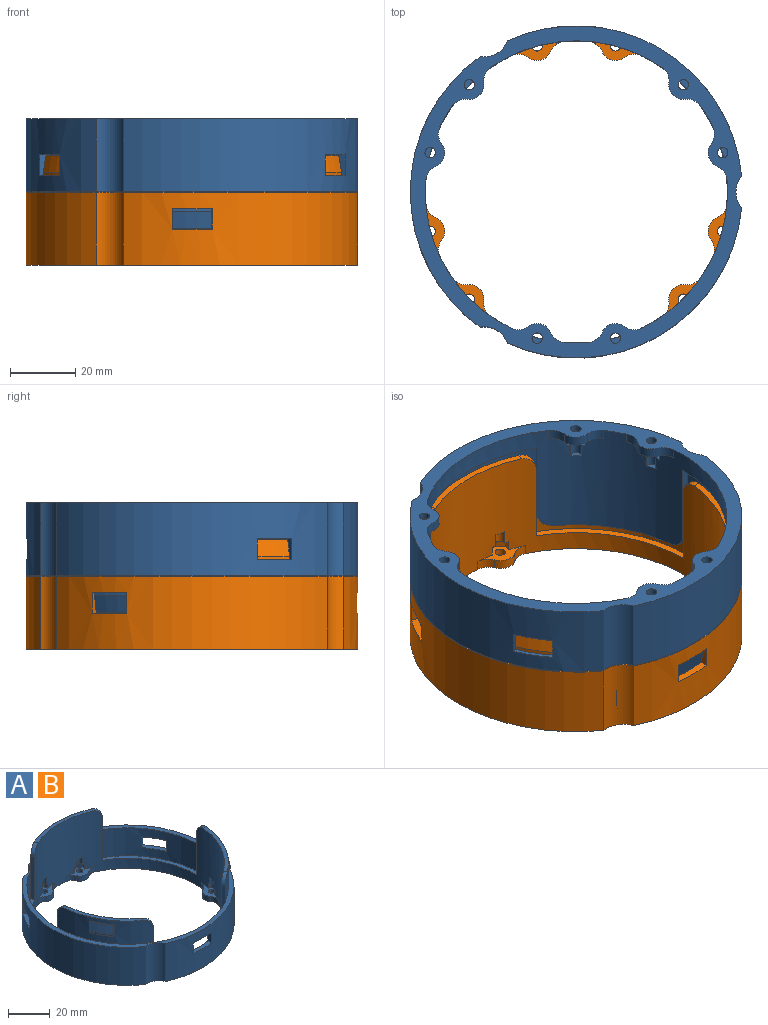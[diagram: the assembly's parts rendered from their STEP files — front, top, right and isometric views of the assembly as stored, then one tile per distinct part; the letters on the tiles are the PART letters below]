
ASSEMBLY  parts=2 mates=1
PART A: 135 faces, bbox 101.8x102x36 mm
  f0: cylinder r=51mm len=71.96mm, axis (0,0,-1), area 2097.8mm2, adj f1,f5,f6,f7,f8,f29,f35,f53
  f1: cylinder r=7.5mm len=22.4mm, axis (0,0,-1), area 235.6mm2, adj f0,f2,f29,f35
  f2: cylinder r=51mm len=83.1mm, axis (0,0,-1), area 2097.8mm2, adj f1,f3,f9,f10,f11,f12,f29,f35
  f3: cylinder r=7.5mm len=22.4mm, axis (0,0,-1), area 235.6mm2, adj f2,f4,f29,f35
  f4: cylinder r=51mm len=71.96mm, axis (0,0,-1), area 2097.8mm2, adj f3,f29,f35,f49,f50,f51,f52,f53
  f5: plane 11.86x8.24mm, normal (0,0,1), area 29.6mm2, adj f0,f7,f8,f37
  f6: plane 11.86x8.24mm, normal (0,0,-1), area 29.6mm2, adj f0,f7,f8,f37
  f7: plane 6.3x2.09mm, normal (0.5,-0.87,0), area 15.2mm2, adj f0,f5,f6,f37
  f8: plane 6.3x2.09mm, normal (-0.5,0.87,0), area 15.2mm2, adj f0,f5,f6,f37
  f9: plane 11.86x8.24mm, normal (0,0,1), area 29.6mm2, adj f2,f11,f12,f44
  f10: plane 11.86x8.24mm, normal (0,0,-1), area 29.6mm2, adj f2,f11,f12,f44
  f11: plane 6.3x2.09mm, normal (0.5,0.87,0), area 15.2mm2, adj f2,f9,f10,f44
  f12: plane 6.3x2.09mm, normal (-0.5,-0.87,0), area 15.2mm2, adj f2,f9,f10,f44
  f13: cylinder r=48.6mm len=48.97mm, axis (0,0,1), area 763.9mm2, adj f29,f41,f42,f43,f49,f50,f51,f52
  f14: cylinder r=49.81mm len=10.39mm, axis (0,0,1), area 12mm2, adj f15,f17,f18,f133
  f15: plane 6x1.23mm, normal (-0.5,0.87,0), area 6mm2, adj f14,f16,f18,f30,f133
  f16: plane 10.6x6.36mm, normal (0,0,1), area 5mm2, adj f15,f17,f30,f133
  f17: plane 6x1.23mm, normal (0.5,-0.87,0), area 6mm2, adj f14,f16,f18,f30,f133
  f18: plane 11.1x7.23mm, normal (0,0,-1), area 17mm2, adj f14,f15,f17,f30
  f19: cylinder r=49.81mm len=10.39mm, axis (0,0,1), area 12mm2, adj f20,f22,f23,f134
  f20: plane 6x1.23mm, normal (-0.5,-0.87,0), area 6mm2, adj f19,f21,f23,f36,f134
  f21: plane 10.6x6.36mm, normal (0,0,1), area 5mm2, adj f20,f22,f36,f134
  f22: plane 6x1.23mm, normal (0.5,0.87,0), area 6mm2, adj f19,f21,f23,f36,f134
  f23: plane 11.1x7.23mm, normal (0,0,-1), area 17mm2, adj f19,f20,f22,f36
  f24: plane 6x1.43mm, normal (1,0,0), area 6mm2, adj f26,f27,f28,f48,f132
  f25: plane 6x1.43mm, normal (-1,0,0), area 6mm2, adj f26,f27,f28,f48,f132
  f26: plane 12x0.79mm, normal (0,0,1), area 5mm2, adj f24,f25,f28,f132
  f27: plane 12x1.79mm, normal (0,0,-1), area 17mm2, adj f24,f25,f28,f48
  f28: cylinder r=48.4mm len=48.03mm, axis (0,0,-1), area 600.6mm2, adj f24,f25,f26,f27,f29,f33,f38,f45
  f29: plane 102x101.77mm, normal (0,0,1), area 741.6mm2, adj f0,f1,f2,f3,f4,f13,f28,f30
  f30: cylinder r=48.4mm len=41.6mm, axis (0,0,-1), area 600.6mm2, adj f15,f16,f17,f18,f29,f31,f41,f46
  f31: plane 33.87x20.56mm, normal (0,0,1), area 78.4mm2, adj f30,f34,f54,f56
  f32: plane 33.87x20.56mm, normal (0,0,1), area 78.4mm2, adj f34,f36,f57,f58
  f33: plane 39.09x5.87mm, normal (0,0,1), area 78.4mm2, adj f28,f34,f55,f59
  f34: cylinder r=46.4mm len=92.8mm, axis (0,0,-1), area 5569.6mm2, adj f31,f32,f33,f35,f38,f39,f40,f41
  f35: plane 102x101.77mm, normal (0,0,-1), area 1526.6mm2, adj f0,f1,f2,f3,f4,f34,f53,f61
  f36: cylinder r=48.4mm len=41.6mm, axis (0,0,-1), area 600.6mm2, adj f20,f21,f22,f23,f29,f32,f39,f42
  f37: cylinder r=48.6mm len=42.41mm, axis (0,0,1), area 763.9mm2, adj f5,f6,f7,f8,f29,f38,f39,f40
  f38: plane 25x1.91mm, normal (0.87,-0.5,0), area 53.3mm2, adj f28,f29,f34,f37,f40,f59
  f39: plane 25x2.2mm, normal (0,1,0), area 53.3mm2, adj f29,f34,f36,f37,f40,f58
  f40: plane 42.41x25.58mm, normal (0,0,1), area 110.3mm2, adj f34,f37,f38,f39
  f41: plane 25x1.9mm, normal (0.86,-0.5,0), area 53.3mm2, adj f13,f29,f30,f34,f43,f56
  f42: plane 25x1.9mm, normal (-0.86,-0.5,0), area 53.3mm2, adj f13,f29,f34,f36,f43,f57
  f43: plane 48.97x8.52mm, normal (0,0,1), area 110.3mm2, adj f13,f34,f41,f42
  f44: cylinder r=48.6mm len=42.41mm, axis (0,0,1), area 763.9mm2, adj f9,f10,f11,f12,f29,f45,f46,f47
  f45: plane 25x1.91mm, normal (-0.87,-0.5,0), area 53.3mm2, adj f28,f29,f34,f44,f47,f55
  f46: plane 25x2.2mm, normal (0,1,0), area 53.3mm2, adj f29,f30,f34,f44,f47,f54
  f47: plane 42.41x25.58mm, normal (0,0,1), area 110.3mm2, adj f34,f44,f45,f46
  f48: cylinder r=49.81mm len=12mm, axis (0,0,1), area 12mm2, adj f24,f25,f27,f132
  f49: plane 12.3x2.79mm, normal (0,0,1), area 29.6mm2, adj f4,f13,f51,f52
  f50: plane 12.3x2.79mm, normal (0,0,-1), area 29.6mm2, adj f4,f13,f51,f52
  f51: plane 6.3x2.42mm, normal (-1,0,0), area 15.2mm2, adj f4,f13,f49,f50
  f52: plane 6.3x2.42mm, normal (1,0,0), area 15.2mm2, adj f4,f13,f49,f50
  f53: cylinder r=7.5mm len=22.4mm, axis (0,0,-1), area 235.6mm2, adj f0,f4,f29,f35
  f54: cylinder r=5mm len=5.01mm, axis (1,0,0), area 15.7mm2, adj f30,f31,f34,f46
  f55: cylinder r=5mm len=5.47mm, axis (-0.5,0.87,0), area 15.7mm2, adj f28,f33,f34,f45
  f56: cylinder r=5mm len=5.46mm, axis (-0.5,-0.86,0), area 15.7mm2, adj f30,f31,f34,f41
  f57: cylinder r=5mm len=5.46mm, axis (-0.5,0.86,0), area 15.7mm2, adj f32,f34,f36,f42
  f58: cylinder r=5mm len=5.01mm, axis (1,0,0), area 15.7mm2, adj f32,f34,f36,f39
  f59: cylinder r=5mm len=5.47mm, axis (-0.5,-0.87,0), area 15.7mm2, adj f28,f33,f34,f38
  f60: plane 16.27x7.67mm, normal (0,0,1), area 41.3mm2, adj f34,f61,f83,f84,f85,f86,f119,f130
  f61: cylinder r=4.49mm len=6.87mm, axis (0,0,-1), area 24.6mm2, adj f35,f60,f130,f131
  f62: plane 16.27x7.67mm, normal (0,0,1), area 41.3mm2, adj f34,f63,f73,f74,f75,f76,f118,f128
  f63: cylinder r=4.49mm len=6.87mm, axis (0,0,-1), area 24.6mm2, adj f35,f62,f128,f129
  f64: plane 11.91x11.91mm, normal (0,0,1), area 41.3mm2, adj f34,f65,f93,f94,f95,f96,f117,f126
  f65: cylinder r=4.49mm len=5.07mm, axis (0,0,-1), area 24.6mm2, adj f35,f64,f126,f127
  f66: plane 16.27x7.67mm, normal (0,0,1), area 41.3mm2, adj f34,f67,f88,f89,f90,f91,f116,f124
  f67: cylinder r=4.49mm len=6.87mm, axis (0,0,-1), area 24.6mm2, adj f35,f66,f124,f125
  f68: plane 16.27x7.67mm, normal (0,0,1), area 41.3mm2, adj f34,f69,f98,f99,f100,f101,f115,f122
  f69: cylinder r=4.49mm len=6.87mm, axis (0,0,-1), area 24.6mm2, adj f35,f68,f122,f123
  f70: plane 11.91x11.91mm, normal (0,0,1), area 41.3mm2, adj f34,f71,f78,f79,f80,f81,f114,f120
  f71: cylinder r=4.49mm len=5.07mm, axis (0,0,-1), area 24.6mm2, adj f35,f70,f120,f121
  f72: plane 5.98x4.11mm, normal (0,0,-1), area 10.5mm2, adj f34,f73,f74,f75,f76,f112
  f73: plane 3x1.78mm, normal (-0.97,-0.26,0), area 5.5mm2, adj f34,f62,f72,f76
  f74: plane 3x1.78mm, normal (0.97,0.26,0), area 5.5mm2, adj f34,f62,f72,f75
  f75: plane 3x2.33mm, normal (0.71,-0.71,0), area 9.9mm2, adj f62,f72,f74,f76
  f76: plane 3.18x3mm, normal (-0.26,-0.97,0), area 9.9mm2, adj f62,f72,f73,f75
  f77: plane 5.33x5.33mm, normal (0,0,-1), area 10.5mm2, adj f34,f78,f79,f80,f81,f110
  f78: plane 3x1.3mm, normal (0.71,-0.71,0), area 5.5mm2, adj f34,f70,f77,f80
  f79: plane 3x1.3mm, normal (-0.71,0.71,0), area 5.5mm2, adj f34,f70,f77,f81
  f80: plane 3.18x3mm, normal (0.97,0.26,0), area 9.9mm2, adj f70,f77,f78,f81
  f81: plane 3.18x3mm, normal (0.26,0.97,0), area 9.9mm2, adj f70,f77,f79,f80
  f82: plane 5.98x4.11mm, normal (0,0,-1), area 10.5mm2, adj f34,f83,f84,f85,f86,f108
  f83: plane 3x1.78mm, normal (-0.97,0.26,0), area 5.5mm2, adj f34,f60,f82,f86
  f84: plane 3x1.78mm, normal (0.97,-0.26,0), area 5.5mm2, adj f34,f60,f82,f85
  f85: plane 3.18x3mm, normal (0.26,-0.97,0), area 9.9mm2, adj f60,f82,f84,f86
  f86: plane 3x2.33mm, normal (-0.71,-0.71,0), area 9.9mm2, adj f60,f82,f83,f85
  f87: plane 5.98x4.11mm, normal (0,0,-1), area 10.5mm2, adj f34,f88,f89,f90,f91,f106
  f88: plane 3x1.78mm, normal (0.26,0.97,0), area 5.5mm2, adj f34,f66,f87,f90
  f89: plane 3x1.78mm, normal (-0.26,-0.97,0), area 5.5mm2, adj f34,f66,f87,f91
  f90: plane 3x2.33mm, normal (-0.71,0.71,0), area 9.9mm2, adj f66,f87,f88,f91
  f91: plane 3.18x3mm, normal (-0.97,-0.26,0), area 9.9mm2, adj f66,f87,f89,f90
  f92: plane 5.33x5.33mm, normal (0,0,-1), area 10.5mm2, adj f34,f93,f94,f95,f96,f104
  f93: plane 3x1.3mm, normal (0.71,0.71,0), area 5.5mm2, adj f34,f64,f92,f96
  f94: plane 3x1.3mm, normal (-0.71,-0.71,0), area 5.5mm2, adj f34,f64,f92,f95
  f95: plane 3.18x3mm, normal (-0.97,0.26,0), area 9.9mm2, adj f64,f92,f94,f96
  f96: plane 3.18x3mm, normal (-0.26,0.97,0), area 9.9mm2, adj f64,f92,f93,f95
  f97: plane 5.98x4.11mm, normal (0,0,-1), area 10.5mm2, adj f34,f98,f99,f100,f101,f102
  f98: plane 3x1.78mm, normal (0.26,-0.97,0), area 5.5mm2, adj f34,f68,f97,f101
  f99: plane 3x1.78mm, normal (-0.26,0.97,0), area 5.5mm2, adj f34,f68,f97,f100
  f100: plane 3x2.33mm, normal (0.71,0.71,0), area 9.9mm2, adj f68,f97,f99,f101
  f101: plane 3.18x3mm, normal (0.97,-0.26,0), area 9.9mm2, adj f68,f97,f98,f100
  f102: cylinder r=1.6mm len=4mm, axis (0,0,-1), area 21.2mm2, adj f34,f97,f103
  f103: plane 3.18x2.14mm, normal (0,0,-1), area 4.4mm2, adj f34,f102
  f104: cylinder r=1.6mm len=4mm, axis (0,0,-1), area 21.2mm2, adj f34,f92,f105
  f105: plane 2.82x2.82mm, normal (0,0,-1), area 4.4mm2, adj f34,f104
  f106: cylinder r=1.6mm len=4mm, axis (0,0,-1), area 21.2mm2, adj f34,f87,f107
  f107: plane 3.18x2.14mm, normal (0,0,-1), area 4.4mm2, adj f34,f106
  f108: cylinder r=1.6mm len=4mm, axis (0,0,-1), area 21.2mm2, adj f34,f82,f109
  f109: plane 3.18x2.14mm, normal (0,0,-1), area 4.4mm2, adj f34,f108
  f110: cylinder r=1.6mm len=4mm, axis (0,0,-1), area 21.2mm2, adj f34,f77,f111
  f111: plane 2.82x2.82mm, normal (0,0,-1), area 4.4mm2, adj f34,f110
  f112: cylinder r=1.6mm len=4mm, axis (0,0,-1), area 21.2mm2, adj f34,f72,f113
  f113: plane 3.18x2.14mm, normal (0,0,-1), area 4.4mm2, adj f34,f112
  f114: cylinder r=1.6mm len=3.2mm, axis (0,0,-1), area 30.2mm2, adj f35,f70
  f115: cylinder r=1.6mm len=3.2mm, axis (0,0,-1), area 30.2mm2, adj f35,f68
  f116: cylinder r=1.6mm len=3.2mm, axis (0,0,-1), area 30.2mm2, adj f35,f66
  f117: cylinder r=1.6mm len=3.2mm, axis (0,0,-1), area 30.2mm2, adj f35,f64
  f118: cylinder r=1.6mm len=3.2mm, axis (0,0,-1), area 30.2mm2, adj f35,f62
  f119: cylinder r=1.6mm len=3.2mm, axis (0,0,-1), area 30.2mm2, adj f35,f60
  f120: cylinder r=5mm len=4.76mm, axis (0,0,-1), area 16.4mm2, adj f34,f35,f70,f71
  f121: cylinder r=5mm len=4.76mm, axis (0,0,1), area 16.4mm2, adj f34,f35,f70,f71
  f122: cylinder r=5mm len=4.22mm, axis (0,0,-1), area 16.4mm2, adj f34,f35,f68,f69
  f123: cylinder r=5mm len=5.18mm, axis (0,0,1), area 16.4mm2, adj f34,f35,f68,f69
  f124: cylinder r=5mm len=5.18mm, axis (0,0,-1), area 16.4mm2, adj f34,f35,f66,f67
  f125: cylinder r=5mm len=4.22mm, axis (0,0,1), area 16.4mm2, adj f34,f35,f66,f67
  f126: cylinder r=5mm len=4.76mm, axis (0,0,-1), area 16.4mm2, adj f34,f35,f64,f65
  f127: cylinder r=5mm len=4.76mm, axis (0,0,1), area 16.4mm2, adj f34,f35,f64,f65
  f128: cylinder r=5mm len=4.22mm, axis (0,0,-1), area 16.4mm2, adj f34,f35,f62,f63
  f129: cylinder r=5mm len=5.18mm, axis (0,0,1), area 16.4mm2, adj f34,f35,f62,f63
  f130: cylinder r=5mm len=5.18mm, axis (0,0,-1), area 16.4mm2, adj f34,f35,f60,f61
  f131: cylinder r=5mm len=4.22mm, axis (0,0,1), area 16.4mm2, adj f34,f35,f60,f61
  f132: cone r=48.81mm half-angle=11.3deg, axis (0,0,-1), area 61.3mm2, adj f24,f25,f26,f48
  f133: cone r=48.81mm half-angle=11.3deg, axis (0,0,-1), area 61.3mm2, adj f14,f15,f16,f17
  f134: cone r=48.81mm half-angle=11.3deg, axis (0,0,-1), area 61.3mm2, adj f19,f20,f21,f22
PART B: same geometry as A
PLACE A rot(axis=(1,0,0),180deg) t=(0,0,45)mm
PLACE B at identity
MATE fastened B.f13 <-> A.f13  axis (0,0,1) through (0,0,22.4)mm
